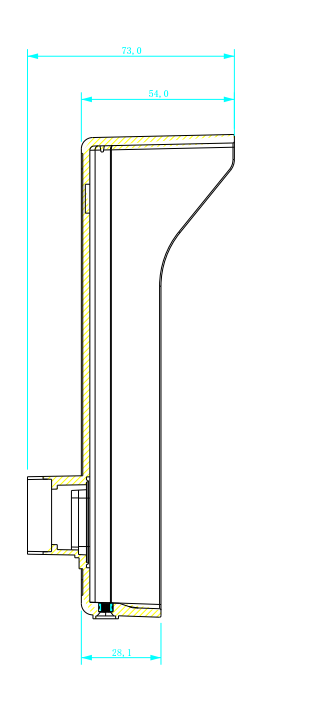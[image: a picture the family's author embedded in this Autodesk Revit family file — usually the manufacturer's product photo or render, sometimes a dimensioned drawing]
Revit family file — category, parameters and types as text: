
# Revit family: SP-03F + SP-SP
name_source: partatom
category: Устройства связи
units: mm (PartAtom-declared; Revit-internal decimal feet)

## family parameters
Всегда вертикально = Нет
На основе рабочей плоскости = Да
Общий = Да
При загрузке вырезать с полостями = Нет
Размер круглого соединителя = Использовать диаметр
Сохранять ориентацию аннотаций = Нет
Тип детали = Нормальный
Точка расчета площади = Нет

## types (1)
- SP-03F с аудиотрубкой SP-SP
    ADSK_URL документации изделия = https://drive.google.com
    ADSK_URL страницы изделия = https://bas-ip.com
    ADSK_Версия Revit = Revit 2020
    ADSK_Единица измерения = шт
    ADSK_Завод-изготовитель = BAS-IP
    ADSK_Классификация нагрузок = Абонентское аудиоустройство
    ADSK_Количество фаз = 1
    ADSK_Коэффициент мощности = 0.9
    ADSK_Марка = SP-03F с аудиотрубкой SP-SP
    ADSK_Наименование = Абонентское аудиоустройство SP-03F с аудиотрубкой SP-SP
    ADSK_Наименование краткое = SP-03F с аудиотрубкой SP-SP
    ADSK_Напряжение = 12 В
    ADSK_Номинальная мощность = 0 Вт
    ADSK_Полная мощность = 0 В·А
    ADSK_Размер_Длина = 185 мм
    ADSK_Размер_Толщина = 28 мм
    ADSK_Размер_Ширина = 166 мм
    BIM library = https://bimlib.ru
    URL = https://www.bas-ip.ru
    Аудиотрубка SP-SP, размеры = 60х185 мм
    Бесшумный режим = Да
    Вес брутто аудиотрубки SP-SP = 0.46 кг
    Вызов лифта на этаж = Да
    Габаритные размеры = 166×185×28 мм
    Группа модели = Абонентское аудиоустройство SP-03F с аудиотрубкой SP-SP
    Дополнительная функция = Кнопка звонка
    Звонки консьержу = Да
    Изготовитель = BAS-IP
    Изображение типоразмера = <Нет>
    Источник питания = PoE, +12 V DC (+11% -6%)
    Количество клавиш управления = 6
    Количество поддерживаемых учетных записей VoIP = 1
    Корпус = Пластик
    Метод конфигурации и программирования = WEB-интерфейс
    Модуль Wi-Fi = Да, для подключения к локальной сети
    Описание = Абонентское аудиоустройство SP-03F - Абонентское IP аудио устройство с поддержкой SIP, P2P и внутреннего протокола BAS-IP. Дополнителная аудиотрубка, которая подключается непосредственно к абонентскому аудиоустройству SP-03. Это решение идеально подходит для тех, кто желает конфиденциальности в разговорах.
    Открытие замка = Да
    Отметка по умолчанию = 0 мм
    Отображение различных состояний устройства с помощью светодиодов = Да
    Переадресация звонков = Да
    Поддерживаемый тип кодека = G.711μ/A
    Поддержка внутреннего протокола BAS-IP = Да
    Поддержка протокола SIP 2.0, для организации связи с любым VoIP оборудованием, поддерживающим этот протокол = Да
    Подключение к сети = 1 PoE порт IEEE 802.3af
    Размеры абонентского аудиоустройства = 106×185×28 мм
    Режим "Не беспокоить" = Да
    Способ установки = Настенный монтаж
    Тип поддерживаемого протокола = IPv4
    Цветовое решение = Черный, белый
